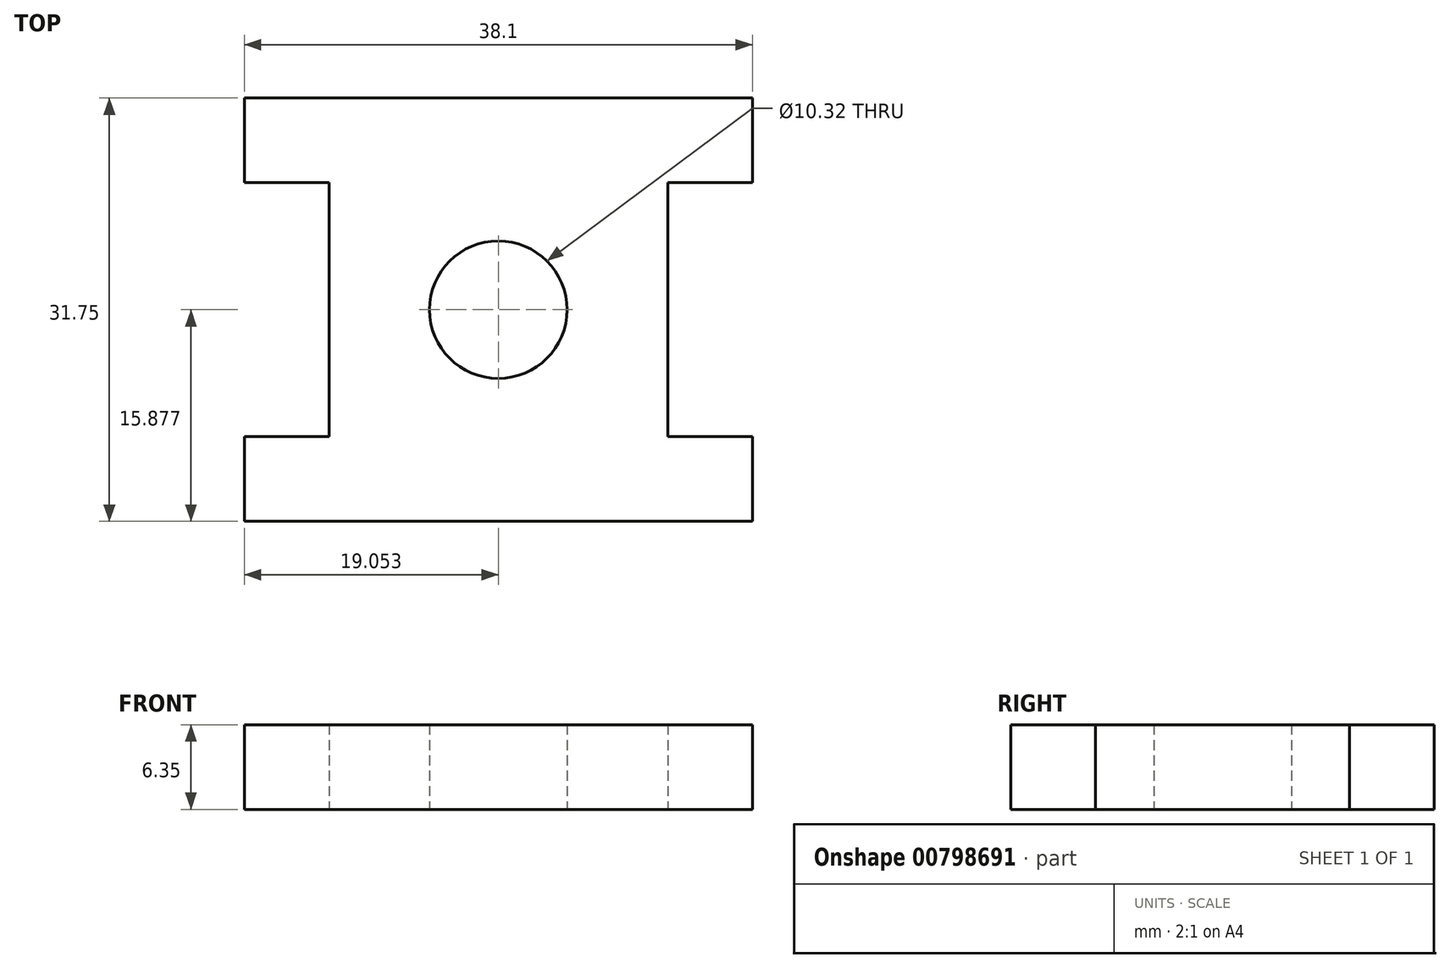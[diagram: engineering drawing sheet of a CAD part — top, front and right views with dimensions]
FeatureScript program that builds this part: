
annotation { "Feature Type Name" : "Feature", "Feature Type Description" : "" }
export const myFeature = defineFeature(function(context is Context, id is Id, definition is map)
    precondition{}
    {
        {
            var Q0;
            Q0=qCreatedBy(makeId("Top.planeOp"),FACE);
            var sketch = newSketch(context, id + "F0", { "sketchPlane" : qUnion([Q0])});
            skLineSegment(sketch, "E0.bottom", {"start": v(-83.92, -68.93) * mm, "end": v(-45.82, -68.93) * mm});
            skLineSegment(sketch, "E0.top", {"start": v(-83.92, -37.18) * mm, "end": v(-45.82, -37.18) * mm});
            skLineSegment(sketch, "E0.left", {"start": v(-83.92, -68.93) * mm, "end": v(-83.92, -62.58) * mm});
            skLineSegment(sketch, "E0.right", {"start": v(-45.82, -68.93) * mm, "end": v(-45.82, -62.58) * mm});
            skLineSegment(sketch, "E1.bottom", {"start": v(-83.92, -62.58) * mm, "end": v(-77.57, -62.58) * mm});
            skLineSegment(sketch, "E1.top", {"start": v(-83.92, -43.53) * mm, "end": v(-77.57, -43.53) * mm});
            skLineSegment(sketch, "E1.right", {"start": v(-77.57, -62.58) * mm, "end": v(-77.57, -43.53) * mm});
            skLineSegment(sketch, "E2.bottom", {"start": v(-45.82, -62.58) * mm, "end": v(-52.17, -62.58) * mm});
            skLineSegment(sketch, "E2.top", {"start": v(-45.82, -43.53) * mm, "end": v(-52.17, -43.53) * mm});
            skLineSegment(sketch, "E2.right", {"start": v(-52.17, -62.58) * mm, "end": v(-52.17, -43.53) * mm});
            skLineSegment(sketch, "E3.trimOffspring", {"start": v(-83.92, -43.53) * mm, "end": v(-83.92, -37.18) * mm});
            skLineSegment(sketch, "E4.trimOffspring", {"start": v(-45.82, -43.53) * mm, "end": v(-45.82, -37.18) * mm});
            skCircle(sketch, "E5", {"center": v(-64.87, -53.05) * mm, "radius": 5.16 * mm});
            skSolve(sketch);
        }
        {
            var Q0;
            Q0=makeQuery(id+"F0.imprint","IMPRINT",FACE,{"disambiguationData":[TD([[makeQuery(id+"F0.imprint","IMPRINT",EDGE,{"derivedFrom":sQuery(id+"F0.wireOp",EDGE,"E0.bottom")}),1.0]])]});
            extrude(context, id + "F1", {"entities" : qUnion([Q0]), "depth" : 6.35 * mm, "offsetDistance" : 25.4 * mm});
        }
    });
